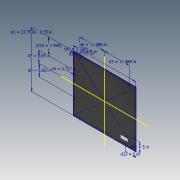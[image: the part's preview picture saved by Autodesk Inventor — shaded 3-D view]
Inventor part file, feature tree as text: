
AUTODESK INVENTOR PART (.ipt)
format: ipt  version: 2020.3 (Build 243373000, 373)  size: 142,848 bytes
history: native  units: in
note: dims shown in document units (in); Inventor stores cm internally (conversion verified against a paired STEP export)
features: extrude x2, hole x2, fillet x2, sketch x1
ambient origin geometry x8: Origin, YZ Plane, XZ Plane, XY Plane, X Axis, Y Axis, Z Axis, Center Point
bodies: Solid1 (feature_tree)
feature tree (7):
  sketch  "Sketch1"  dims[d0=30.475in d1=27.2in d3=0.737in d4=0.737in d5=11.988in d6=11.988in d7=5.65in d8=5.65in d9=3.2495in d10=7.95in d11=0.125in d12=0.0in d13=0.3125in d14=0.75in d15=0.375in d16=0.25in d17=0.5635in d18=1.0in d19=0.8108in d20=0.25in d22=5.0in d23=5.0in d25=0.0in d26=0.0in d28=9.447in d29=3.75in d30=3.5in d31=1.875in d32=0.25in d33=0.128in d34=0.75in d35=0.375in d36=0.25in d37=0.5635in d38=1.0in d39=0.8108in]
  extrude  "Extrusion1"  Depth=27.2in
  hole  "Hole1"  [1 undecoded]
  fillet  "Fillet1"  Radius=0.737in
  extrude  "Extrusion2"  Depth=0.25in
  fillet  "Fillet3"  Radius=11.988in
  hole  "Hole2"  [1 undecoded]
note: 2 required parameter values undecoded (feature->parameter linkage not recoverable at this tier; creation-order binding heuristic only, values carry confidence <= 0.55)
